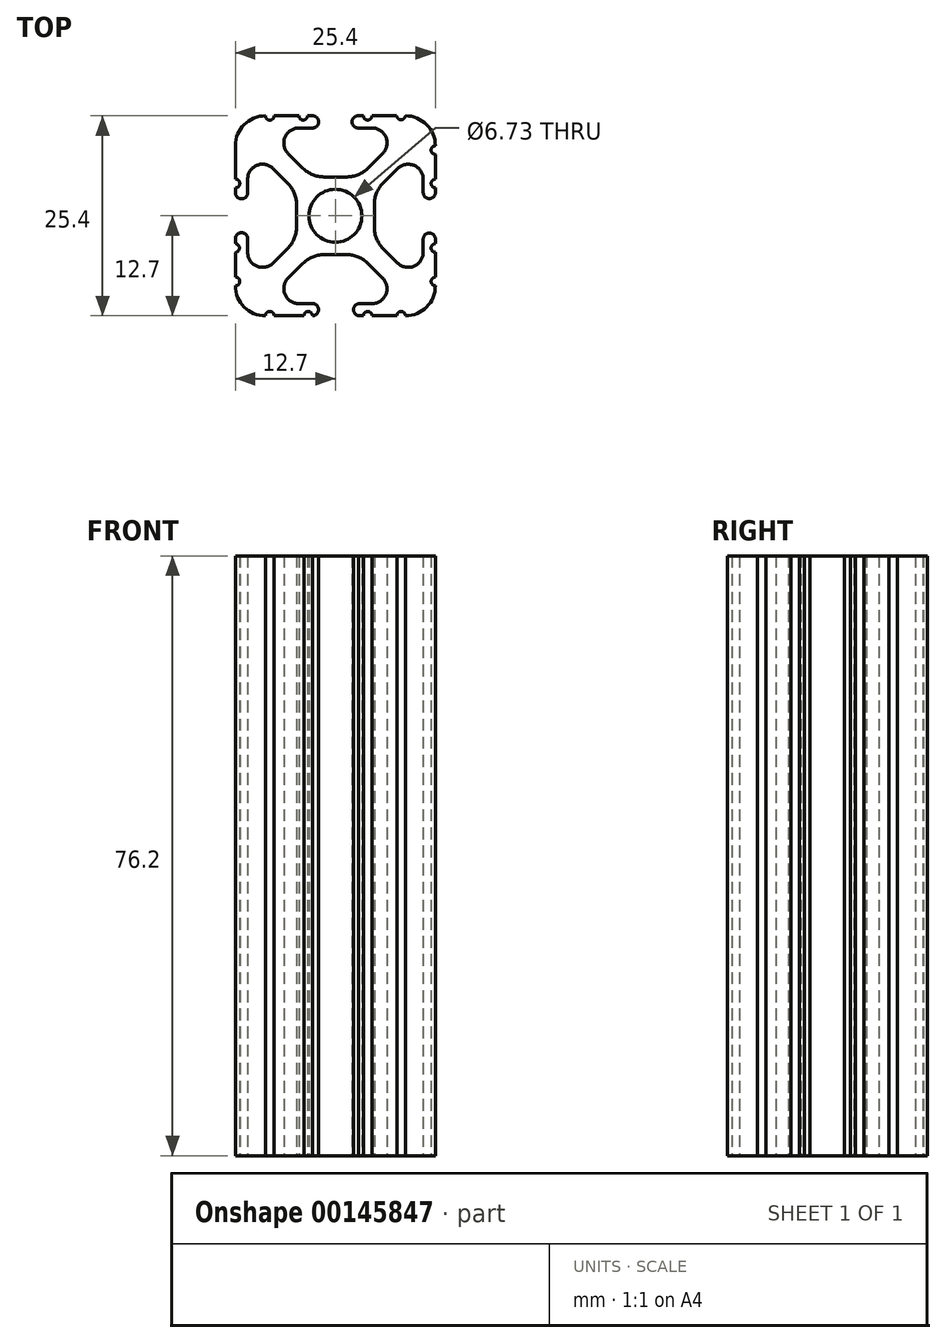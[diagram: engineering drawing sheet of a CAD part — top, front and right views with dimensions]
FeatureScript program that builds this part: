
annotation { "Feature Type Name" : "Feature", "Feature Type Description" : "" }
export const myFeature = defineFeature(function(context is Context, id is Id, definition is map)
    precondition{}
    {
        {
            var Q0;
            Q0=qCreatedBy(makeId("Top.planeOp"),FACE);
            var sketch = newSketch(context, id + "F0", { "sketchPlane" : qUnion([Q0])});
            skCircle(sketch, "E0", {"center": v(-12.7, 12.7) * mm, "radius": 3.36 * mm});
            skLineSegment(sketch, "E1.bottom", {"start": v(-11.24, 17.64) * mm, "end": v(-14.16, 17.64) * mm});
            skLineSegment(sketch, "E1.top", {"start": v(-11.24, 7.76) * mm, "end": v(-14.16, 7.76) * mm});
            skLineSegment(sketch, "E1.left", {"start": v(-7.76, 14.16) * mm, "end": v(-7.76, 11.24) * mm});
            skLineSegment(sketch, "E1.right", {"start": v(-17.64, 14.16) * mm, "end": v(-17.64, 11.24) * mm});
            skPoint(sketch, "E2.visualSharp", {"position": v(-25.4, 25.4) * mm});
            skPoint(sketch, "E3.visualSharp", {"position": v(0, 25.4) * mm});
            skPoint(sketch, "E4.visualSharp", {"position": v(0, 0) * mm});
            skPoint(sketch, "E5.visualSharp", {"position": v(-25.4, 0) * mm});
            skLineSegment(sketch, "E6.0", {"start": v(-18.7, 20.6) * mm, "end": v(-16.85, 18.76) * mm});
            skLineSegment(sketch, "E7.0", {"start": v(-20.6, 18.7) * mm, "end": v(-18.76, 16.85) * mm});
            skPoint(sketch, "E8.orphan", {"position": v(-23.85, 1.55) * mm});
            skPoint(sketch, "E9.orphan", {"position": v(-23.85, 23.85) * mm});
            skPoint(sketch, "E10.orphan", {"position": v(-1.55, 23.85) * mm});
            skPoint(sketch, "E11.orphan", {"position": v(-1.55, 1.55) * mm});
            skLineSegment(sketch, "E12", {"start": v(-8.55, 6.64) * mm, "end": v(-6.7, 4.8) * mm});
            skLineSegment(sketch, "E13.0", {"start": v(-18.7, 4.8) * mm, "end": v(-16.85, 6.64) * mm});
            skLineSegment(sketch, "E14.0", {"start": v(-20.6, 6.7) * mm, "end": v(-18.76, 8.55) * mm});
            skLineSegment(sketch, "E15.0", {"start": v(-8.55, 18.76) * mm, "end": v(-6.7, 20.6) * mm});
            skPoint(sketch, "E16.visualSharp", {"position": v(-23.85, 21.95) * mm});
            skArc(sketch, "E16.filletArc", {"start": v(-20.6, 18.7) * mm, "mid": v(-22.68, 19.1) * mm, "end": v(-23.85, 17.35) * mm});
            skPoint(sketch, "E17.visualSharp", {"position": v(-21.95, 23.85) * mm});
            skArc(sketch, "E17.filletArc", {"start": v(-17.35, 23.85) * mm, "mid": v(-19.1, 22.68) * mm, "end": v(-18.7, 20.6) * mm});
            skPoint(sketch, "E18.visualSharp", {"position": v(-5.34, 23.85) * mm});
            skLineSegment(sketch, "E19", {"start": v(-17.35, 23.85) * mm, "end": v(-15.58, 23.85) * mm});
            skLineSegment(sketch, "E20", {"start": v(-23.85, 17.35) * mm, "end": v(-23.85, 15.62) * mm});
            skLineSegment(sketch, "E21", {"start": v(-8.05, 1.55) * mm, "end": v(-9.78, 1.55) * mm});
            skArc(sketch, "E22.filletArc", {"start": v(-6.7, 20.6) * mm, "mid": v(-6.3, 22.68) * mm, "end": v(-8.05, 23.85) * mm});
            skPoint(sketch, "E23.visualSharp", {"position": v(-1.55, 3.45) * mm});
            skPoint(sketch, "E24.visualSharp", {"position": v(-3.45, 1.55) * mm});
            skArc(sketch, "E24.filletArc", {"start": v(-8.05, 1.55) * mm, "mid": v(-6.3, 2.73) * mm, "end": v(-6.7, 4.8) * mm});
            skArc(sketch, "E25.filletArc", {"start": v(-18.7, 4.8) * mm, "mid": v(-19.1, 2.73) * mm, "end": v(-17.35, 1.55) * mm});
            skArc(sketch, "E26.filletArc", {"start": v(-23.85, 8.05) * mm, "mid": v(-22.68, 6.3) * mm, "end": v(-20.6, 6.7) * mm});
            skLineSegment(sketch, "E27.bottom", {"start": v(-4.9, 0) * mm, "end": v(-8.05, 0) * mm});
            skLineSegment(sketch, "E27.top", {"start": v(-4.92, 25.4) * mm, "end": v(-8.05, 25.4) * mm});
            skLineSegment(sketch, "E27.left", {"start": v(0, 4.9) * mm, "end": v(0, 8.05) * mm});
            skLineSegment(sketch, "E27.right", {"start": v(-25.4, 4.9) * mm, "end": v(-25.4, 8.05) * mm});
            skArc(sketch, "E28.filletArc", {"start": v(-25.4, 3.81) * mm, "mid": v(-24.28, 1.12) * mm, "end": v(-21.59, 0) * mm});
            skArc(sketch, "E29.filletArc", {"start": v(-3.81, 0) * mm, "mid": v(-1.12, 1.12) * mm, "end": v(0, 3.8) * mm});
            skArc(sketch, "E30.filletArc", {"start": v(0, 21.59) * mm, "mid": v(-1.12, 24.28) * mm, "end": v(-3.8, 25.4) * mm});
            skArc(sketch, "E31.filletArc", {"start": v(-21.59, 25.4) * mm, "mid": v(-24.28, 24.28) * mm, "end": v(-25.4, 21.59) * mm});
            skPoint(sketch, "E32.newPointA", {"position": v(-17.64, 7.76) * mm});
            skArc(sketch, "E32.filletArc", {"start": v(-14.16, 7.76) * mm, "mid": v(-15.62, 7.47) * mm, "end": v(-16.85, 6.64) * mm});
            skPoint(sketch, "E33.newPointA", {"position": v(-7.76, 7.76) * mm});
            skArc(sketch, "E33.filletArc", {"start": v(-8.55, 6.64) * mm, "mid": v(-9.78, 7.47) * mm, "end": v(-11.24, 7.76) * mm});
            skArc(sketch, "E34.filletArc", {"start": v(-7.76, 11.24) * mm, "mid": v(-7.47, 9.78) * mm, "end": v(-6.64, 8.55) * mm});
            skArc(sketch, "E35.filletArc", {"start": v(-6.64, 16.85) * mm, "mid": v(-7.47, 15.62) * mm, "end": v(-7.76, 14.16) * mm});
            skPoint(sketch, "E36.newPointB", {"position": v(-7.76, 17.64) * mm});
            skArc(sketch, "E36.filletArc", {"start": v(-11.24, 17.64) * mm, "mid": v(-9.78, 17.93) * mm, "end": v(-8.55, 18.76) * mm});
            skPoint(sketch, "E37.newPointB", {"position": v(-17.64, 17.64) * mm});
            skArc(sketch, "E37.filletArc", {"start": v(-16.85, 18.76) * mm, "mid": v(-15.62, 17.93) * mm, "end": v(-14.16, 17.64) * mm});
            skArc(sketch, "E38.filletArc", {"start": v(-17.64, 14.16) * mm, "mid": v(-17.93, 15.62) * mm, "end": v(-18.76, 16.85) * mm});
            skArc(sketch, "E39.filletArc", {"start": v(-18.76, 8.55) * mm, "mid": v(-17.93, 9.78) * mm, "end": v(-17.64, 11.24) * mm});
            skLineSegment(sketch, "E40", {"start": v(-6.64, 8.55) * mm, "end": v(-4.8, 6.7) * mm});
            skPoint(sketch, "E41.visualSharp", {"position": v(-1.55, 21.95) * mm});
            skArc(sketch, "E42.filletArc", {"start": v(-4.8, 6.7) * mm, "mid": v(-2.73, 6.3) * mm, "end": v(-1.55, 8.05) * mm});
            skLineSegment(sketch, "E43", {"start": v(-1.55, 8.05) * mm, "end": v(-1.55, 9.78) * mm});
            skLineSegment(sketch, "E44", {"start": v(-6.64, 16.85) * mm, "end": v(-4.8, 18.7) * mm});
            skArc(sketch, "E45.filletArc", {"start": v(-1.55, 17.35) * mm, "mid": v(-2.73, 19.1) * mm, "end": v(-4.8, 18.7) * mm});
            skArc(sketch, "E46", {"start": v(-23.85, 9.78) * mm, "mid": v(-24.63, 10.56) * mm, "end": v(-25.4, 9.78) * mm});
            skArc(sketch, "E47", {"start": v(-25.4, 15.62) * mm, "mid": v(-24.63, 14.86) * mm, "end": v(-23.85, 15.62) * mm});
            skArc(sketch, "E48", {"start": v(-15.62, 23.85) * mm, "mid": v(-14.83, 24.63) * mm, "end": v(-15.62, 25.4) * mm});
            skArc(sketch, "E49", {"start": v(-9.78, 25.4) * mm, "mid": v(-10.6, 24.63) * mm, "end": v(-9.78, 23.85) * mm});
            skArc(sketch, "E50", {"start": v(-1.55, 15.62) * mm, "mid": v(-0.77, 14.88) * mm, "end": v(0, 15.62) * mm});
            skArc(sketch, "E51", {"start": v(0, 9.78) * mm, "mid": v(-0.77, 10.5) * mm, "end": v(-1.55, 9.78) * mm});
            skArc(sketch, "E52", {"start": v(-9.78, 1.55) * mm, "mid": v(-10.4, 0.77) * mm, "end": v(-9.78, 0) * mm});
            skArc(sketch, "E53", {"start": v(-15.62, 0) * mm, "mid": v(-14.85, 0.77) * mm, "end": v(-15.62, 1.55) * mm});
            skLineSegment(sketch, "E54.trimOffspring", {"start": v(-15.62, 1.55) * mm, "end": v(-17.35, 1.55) * mm});
            skLineSegment(sketch, "E55.trimOffspring", {"start": v(-16.7, 0) * mm, "end": v(-20.5, 0) * mm});
            skLineSegment(sketch, "E56.trimOffspring", {"start": v(-1.55, 15.62) * mm, "end": v(-1.55, 17.35) * mm});
            skLineSegment(sketch, "E57.trimOffspring", {"start": v(0, 15.62) * mm, "end": v(0, 16.26) * mm});
            skLineSegment(sketch, "E58.trimOffspring", {"start": v(-23.85, 9.78) * mm, "end": v(-23.85, 8.05) * mm});
            skLineSegment(sketch, "E59.trimOffspring", {"start": v(-25.4, 15.62) * mm, "end": v(-25.4, 16.26) * mm});
            skLineSegment(sketch, "E60.trimOffspring", {"start": v(-9.86, 23.85) * mm, "end": v(-8.05, 23.85) * mm});
            skLineSegment(sketch, "E61.trimOffspring", {"start": v(-15.58, 25.4) * mm, "end": v(-16.25, 25.4) * mm});
            skPoint(sketch, "E62.start.orphan", {"position": v(-15.62, 17.93) * mm});
            skPoint(sketch, "E63.start.orphan", {"position": v(-9.78, 17.93) * mm});
            skPoint(sketch, "E64.start.orphan", {"position": v(-7.47, 15.62) * mm});
            skPoint(sketch, "E65.start.orphan", {"position": v(-7.47, 9.78) * mm});
            skPoint(sketch, "E66.start.orphan", {"position": v(-17.93, 15.62) * mm});
            skPoint(sketch, "E67.start.orphan", {"position": v(-17.93, 9.78) * mm});
            skPoint(sketch, "E68.start.orphan", {"position": v(-9.78, 7.47) * mm});
            skPoint(sketch, "E69.start.orphan", {"position": v(-15.62, 7.47) * mm});
            skPoint(sketch, "E70.endSnap0", {"position": v(0, 18.6) * mm});
            skPoint(sketch, "E71.startSnap0", {"position": v(-1.55, 8.92) * mm});
            skArc(sketch, "E72", {"start": v(-4.92, 25.4) * mm, "mid": v(-4.37, 24.9) * mm, "end": v(-3.81, 25.4) * mm});
            skArc(sketch, "E73", {"start": v(-9.14, 25.4) * mm, "mid": v(-8.6, 24.86) * mm, "end": v(-8.05, 25.4) * mm});
            skArc(sketch, "E74", {"start": v(-17.35, 25.4) * mm, "mid": v(-16.8, 24.86) * mm, "end": v(-16.25, 25.4) * mm});
            skArc(sketch, "E75", {"start": v(-21.59, 25.4) * mm, "mid": v(-21.04, 24.85) * mm, "end": v(-20.49, 25.4) * mm});
            skLineSegment(sketch, "E76", {"start": v(-25.4, 21.59) * mm, "end": v(-25.4, 20.5) * mm});
            skArc(sketch, "E77", {"start": v(-25.4, 16.26) * mm, "mid": v(-24.84, 16.8) * mm, "end": v(-25.4, 17.35) * mm});
            skArc(sketch, "E78", {"start": v(-25.4, 8.05) * mm, "mid": v(-24.9, 8.6) * mm, "end": v(-25.4, 9.15) * mm});
            skArc(sketch, "E79", {"start": v(-25.4, 3.81) * mm, "mid": v(-24.85, 4.36) * mm, "end": v(-25.4, 4.9) * mm});
            skArc(sketch, "E80", {"start": v(-20.5, 0) * mm, "mid": v(-21.04, 0.55) * mm, "end": v(-21.59, 0) * mm});
            skArc(sketch, "E81", {"start": v(-15.62, 0) * mm, "mid": v(-16.16, 0.54) * mm, "end": v(-16.7, 0) * mm});
            skArc(sketch, "E82", {"start": v(-8.05, 0) * mm, "mid": v(-8.6, 0.55) * mm, "end": v(-9.15, 0) * mm});
            skArc(sketch, "E83", {"start": v(-3.81, 0) * mm, "mid": v(-4.35, 0.54) * mm, "end": v(-4.9, 0) * mm});
            skLineSegment(sketch, "E84.trimOffspring", {"start": v(-17.35, 25.4) * mm, "end": v(-20.49, 25.4) * mm});
            skLineSegment(sketch, "E85.trimOffspring", {"start": v(-25.4, 17.35) * mm, "end": v(-25.4, 21.59) * mm});
            skLineSegment(sketch, "E86.trimOffspring", {"start": v(-25.4, 9.15) * mm, "end": v(-25.4, 9.78) * mm});
            skLineSegment(sketch, "E87.trimOffspring", {"start": v(-9.15, 0) * mm, "end": v(-9.78, 0) * mm});
            skArc(sketch, "E88", {"start": v(0, 4.9) * mm, "mid": v(-0.54, 4.36) * mm, "end": v(0, 3.8) * mm});
            skArc(sketch, "E89", {"start": v(0, 9.15) * mm, "mid": v(-0.54, 8.6) * mm, "end": v(0, 8.05) * mm});
            skLineSegment(sketch, "E90.trimOffspring", {"start": v(0, 9.15) * mm, "end": v(0, 9.78) * mm});
            skArc(sketch, "E91", {"start": v(0, 21.59) * mm, "mid": v(-0.55, 21.04) * mm, "end": v(0, 20.5) * mm});
            skArc(sketch, "E92", {"start": v(0, 17.35) * mm, "mid": v(-0.55, 16.8) * mm, "end": v(0, 16.26) * mm});
            skLineSegment(sketch, "E93.trimOffspring", {"start": v(0, 17.35) * mm, "end": v(0, 20.5) * mm});
            skLineSegment(sketch, "E94.trimOffspring", {"start": v(-9.14, 25.4) * mm, "end": v(-9.86, 25.4) * mm});
            skSolve(sketch);
        }
        {
            var Q0;
            Q0=qSketchRegion(id+"F0",true);
            extrude(context, id + "F1", {"entities" : qUnion([Q0]), "depth" : 76.2 * mm});
        }
    });
